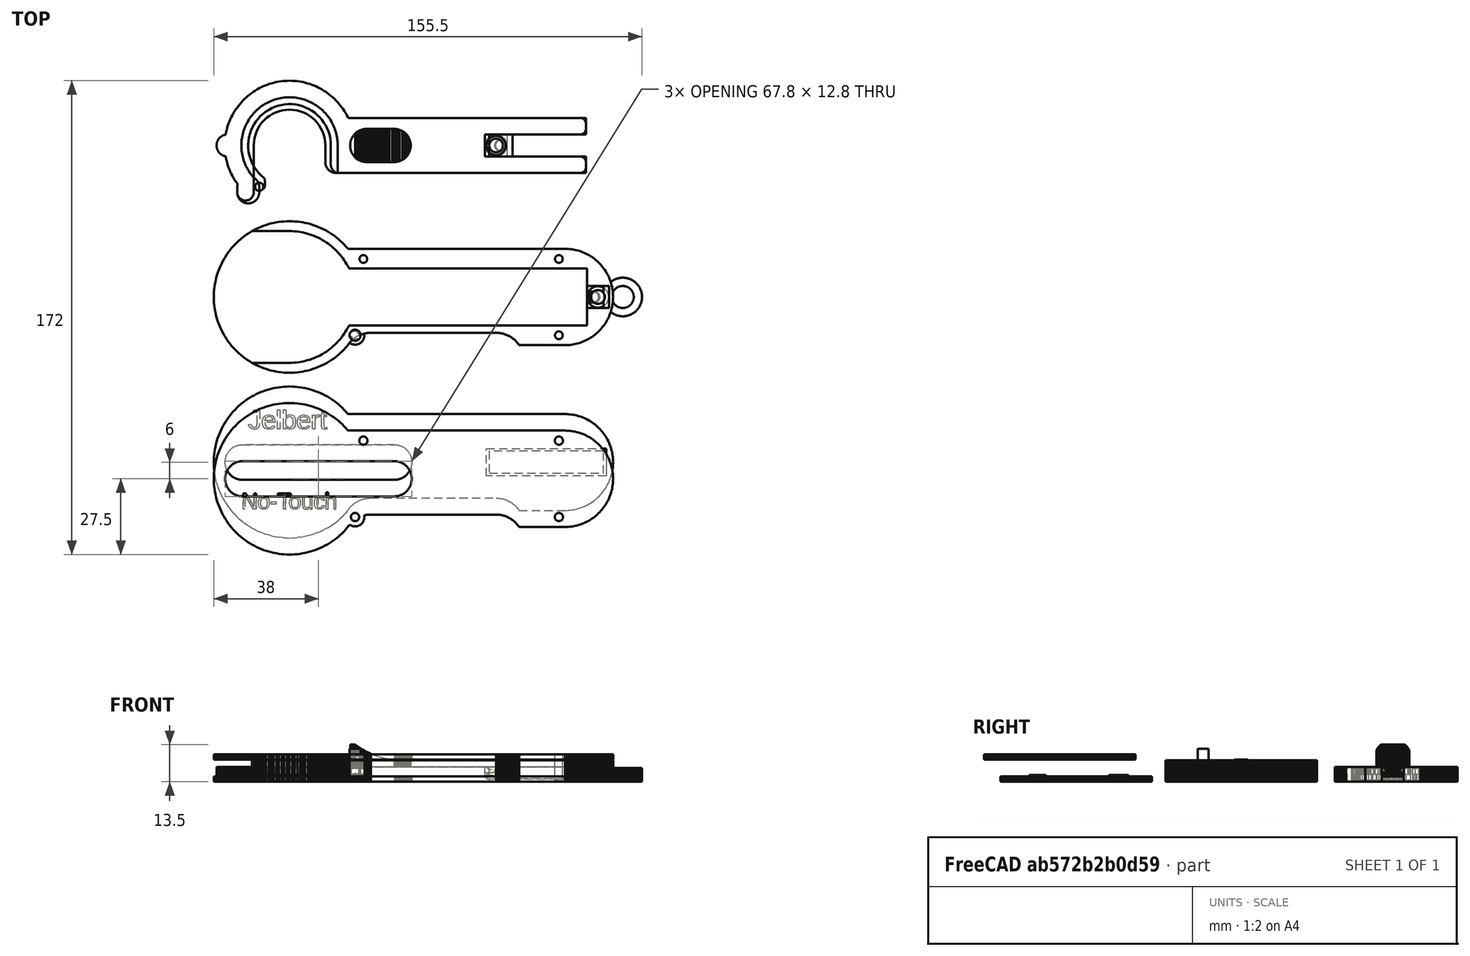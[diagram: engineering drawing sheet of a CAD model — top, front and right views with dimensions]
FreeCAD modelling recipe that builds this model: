
FCSTD DOCUMENT  (FreeCAD 0.18R4 (GitTag))
Label: notouch
License: CreativeCommons Attribution-ShareAlike
LicenseURL: http://creativecommons.org/licenses/by-sa/4.0/
objects: Part::Cylinder×25, Part::Cut×23, Part::Feature×19, Part::MultiFuse×13, Part::Box×13, Part::Fillet×3, Part::Chamfer×3, Part::MultiCommon×2
note: 101 computed .brp shape members not serialized (recipe doc carries the construction recipe); baked Part::Feature solids carry a one-line shape summary decoded from their .brp

FEATURE [Part::Feature] jelbert_no_touch_base_part001_solid001  label="jelbert_no_touch_base_part001 (Solid)001"
  shape: bbox 155.5 x 55 x 7.8 mm, 1307 faces (baked)
FEATURE [Part::Feature] jelbert_no_touch_hook_part001_solid001  label="jelbert_no_touch_hook_part001 (Solid)001"
  shape: bbox 134.1 x 44.5 x 13.5 mm, 1441 faces (baked)
FEATURE [Part::Feature] Cut_solid001  label="jelbert_no_touch_top_part001_01"
  shape: bbox 145 x 55 x 2.5 mm, 996 faces (baked)
FEATURE [Part::Feature] Fusion007002003002  label="soporte_simple014"
  Placement = pos=(91,-56.7,114.8) rot=(0,0,1;0rad)
  shape: bbox 6 x 6 x 6 mm, 8 faces (baked)
FEATURE [Part::Feature] Fusion007002003003  label="soporte_simple015"
  Placement = pos=(20,-56.7,114.8) rot=(0,0,1;0rad)
  shape: bbox 6 x 6 x 6 mm, 8 faces (baked)
FEATURE [Part::Feature] Fusion007002003004  label="soporte_simple016"
  Placement = pos=(91,-84.4,114.8) rot=(0,0,1;0rad)
  shape: bbox 6 x 6 x 6 mm, 8 faces (baked)
FEATURE [Part::Feature] Fusion007002003005  label="soporte_simple017"
  Placement = pos=(17,-84.4,114.8) rot=(0,0,1;0rad)
  shape: bbox 6 x 6 x 6 mm, 8 faces (baked)
FEATURE [Part::Cylinder] Cylinder
  Angle = 360
  AttacherType = Attacher::AttachEngine3D
  Height = 10
  Placement = pos=(26.8,-41.15,2) rot=(0,0,1;0rad)
  Radius = 2
FEATURE [Part::Cylinder] Cylinder001
  Angle = 360
  AttacherType = Attacher::AttachEngine3D
  Height = 10
  Placement = pos=(97.8,-41.15,2) rot=(0,0,1;0rad)
  Radius = 2
FEATURE [Part::Cylinder] Cylinder002
  Angle = 360
  AttacherType = Attacher::AttachEngine3D
  Height = 10
  Placement = pos=(97.8,-68.9,2) rot=(0,0,1;0rad)
  Radius = 2
FEATURE [Part::Cylinder] Cylinder003
  Angle = 360
  AttacherType = Attacher::AttachEngine3D
  Height = 10
  Placement = pos=(23.8,-68.9,2) rot=(0,0,1;0rad)
  Radius = 2
FEATURE [Part::Cylinder] Cylinder004
  Angle = 360
  AttacherType = Attacher::AttachEngine3D
  Height = 7.8
  Placement = pos=(23.8,-68.9,0) rot=(0,0,1;0rad)
  Radius = 3.4
FEATURE [Part::Cylinder] Cylinder005
  Angle = 360
  AttacherType = Attacher::AttachEngine3D
  Height = 10
  Placement = pos=(23.8,-68.9,4) rot=(0,0,1;0rad)
  Radius = 1.5
FEATURE [Part::Feature] jelbert_no_touch_base_part001_solid002  label="jelbert_no_touch_base_part001 (Solid)002"
  shape: bbox 155.5 x 55 x 7.8 mm, 1307 faces (baked)
FEATURE [Part::Cylinder] Cylinder006
  Angle = 360
  AttacherType = Attacher::AttachEngine3D
  Height = 2
  Placement = pos=(23.8,-68.9,8) rot=(0,0,1;0rad)
  Radius = 3.4
FEATURE [Part::MultiFuse] Fusion
  Shapes = -> [jelbert_no_touch_base_part001_solid002,Cylinder004]
FEATURE [Part::Cylinder] Cylinder007
  Angle = 360
  AttacherType = Attacher::AttachEngine3D
  Height = 10
  Placement = pos=(23.8,-68.9,2) rot=(0,0,1;0rad)
  Radius = 2
FEATURE [Part::Cut] Cut
  Base = -> Fusion
  Tool = -> Cylinder003
FEATURE [Part::MultiFuse] Fusion007002003006
  Shapes = -> [Cut,Fusion007002003005]
FEATURE [Part::Cylinder] Cylinder008
  Angle = 360
  AttacherType = Attacher::AttachEngine3D
  Height = 10
  Placement = pos=(26.8,-41.15,2) rot=(0,0,1;0rad)
  Radius = 1.5
FEATURE [Part::Cut] Cut001
  Base = -> Fusion007002003006
  Tool = -> Cylinder
FEATURE [Part::MultiFuse] Fusion007002003007
  Shapes = -> [Cut001,Fusion007002003003]
FEATURE [Part::Cylinder] Cylinder009
  Angle = 360
  AttacherType = Attacher::AttachEngine3D
  Height = 10
  Placement = pos=(97.8,-41.15,3) rot=(0,0,1;0rad)
  Radius = 1.5
FEATURE [Part::Cut] Cut002
  Base = -> Fusion007002003007
  Tool = -> Cylinder001
FEATURE [Part::MultiFuse] Fusion007002003008
  Shapes = -> [Cut002,Fusion007002003002]
FEATURE [Part::Cylinder] Cylinder010
  Angle = 360
  AttacherType = Attacher::AttachEngine3D
  Height = 10
  Placement = pos=(97.8,-68.9,1) rot=(0,0,1;0rad)
  Radius = 1.5
FEATURE [Part::Cut] Cut003
  Base = -> Fusion007002003008
  Tool = -> Cylinder002
FEATURE [Part::MultiFuse] Fusion007002003009  label="base"
  Shapes = -> [Cut003,Fusion007002003004]
FEATURE [Part::Feature] Cut_solid002  label="jelbert_no_touch_top_part001_002"
  shape: bbox 145 x 55 x 2.5 mm, 996 faces (baked)
FEATURE [Part::Box] Box  label="Cube"
  AttacherType = Attacher::AttachEngine3D
  Height = 10
  Length = 175
  Placement = pos=(-39,-152,2) rot=(0,0,1;0rad)
  Width = 67
FEATURE [Part::Cut] Cut004
  Base = -> Cut_solid002
  Tool = -> Box
FEATURE [Part::Box] Box001  label="Cube001"
  AttacherType = Attacher::AttachEngine3D
  Height = 2
  Length = 31
  Placement = pos=(-16,-104,0) rot=(0,0,1;0rad)
  Width = 10
FEATURE [Part::Box] Box002  label="Cube002"
  AttacherType = Attacher::AttachEngine3D
  Height = 2
  Length = 36
  Placement = pos=(-18,-134,0) rot=(0,0,1;0rad)
  Width = 10
FEATURE [Part::Box] Box003  label="Cube003"
  AttacherType = Attacher::AttachEngine3D
  Height = 2
  Length = 45
  Placement = pos=(70,-121,0) rot=(0,0,1;0rad)
  Width = 12
FEATURE [Part::MultiFuse] Fusion007002003010
  Shapes = -> [Cut004,Box001,Box002,Box003]
FEATURE [Part::Feature] Fusion007002003010001  label="tapa_sin_agujeros"
  Placement = pos=(0,60,8) rot=(0,0,1;0rad)
  shape: bbox 145 x 55 x 2 mm, 477 faces (baked)
FEATURE [Part::MultiFuse] Fusion007002003010002  label="tapa_sin_agujeros_1"
  Shapes = -> [Fusion007002003010001,Cylinder006]
FEATURE [Part::Cut] Cut005
  Base = -> Fusion007002003010002
  Tool = -> Cylinder005
FEATURE [Part::Cut] Cut006
  Base = -> Cut005
  Tool = -> Cylinder008
FEATURE [Part::Cut] Cut007
  Base = -> Cut006
  Tool = -> Cylinder009
FEATURE [Part::Cut] Cut008  label="tapa"
  Base = -> Cut007
  Placement = pos=(0,-66,0) rot=(0,0,1;0rad)
  Tool = -> Cylinder010
FEATURE [Part::Feature] jelbert_no_touch_hook_part001_solid002  label="jelbert_no_touch_hook_part001 (Solid)002"
  shape: bbox 134.1 x 44.5 x 13.5 mm, 1441 faces (baked)
FEATURE [Part::Cylinder] Cylinder011
  Angle = 360
  AttacherType = Attacher::AttachEngine3D
  Height = 5.4
  Radius = 18
FEATURE [Part::Cylinder] Cylinder012
  Angle = 360
  AttacherType = Attacher::AttachEngine3D
  Height = 5.4
  Radius = 13
FEATURE [Part::Cut] Cut009
  Base = -> Cylinder011
  Tool = -> Cylinder012
FEATURE [Part::MultiFuse] Fusion007002003010003
  Shapes = -> [jelbert_no_touch_hook_part001_solid002,Cut009]
FEATURE [Part::Box] Box004  label="Cube004"
  AttacherType = Attacher::AttachEngine3D
  Height = 5.4
  Length = 7
  Placement = pos=(15,-10,0) rot=(0,0,1;0rad)
  Width = 7
FEATURE [Part::Cylinder] Cylinder013
  Angle = 360
  AttacherType = Attacher::AttachEngine3D
  Height = 5.4
  Placement = pos=(-11,-15,0) rot=(0,0,1;0rad)
  Radius = 1.5
FEATURE [Part::Feature] Fillet001001  label="medio"
  shape: bbox 134.1 x 44.5 x 13.83 mm, 1304 faces (baked)
FEATURE [Part::Box] Box005  label="Cube005"
  AttacherType = Attacher::AttachEngine3D
  Height = 10
  Length = 24
  Placement = pos=(-9,-21,0) rot=(0,0,1;0rad)
  Width = 21
FEATURE [Part::Cut] Cut010
  Base = -> Fillet001001
  Tool = -> Box005
FEATURE [Part::Fillet] Fillet001002
  Base = -> Cut010
  Edges = 1 edges r=3: [Edge476]
FEATURE [Part::Fillet] Fillet001003
  Base = -> Fillet001002
  Edges = 2 edges r=1: [Edge482,Edge486]
FEATURE [Part::Feature] Fillet001003001  label="medio_final"
  shape: bbox 134.1 x 44.5 x 13.83 mm, 1307 faces (baked)
FEATURE [Part::Cylinder] Cylinder014
  Angle = 360
  AttacherType = Attacher::AttachEngine3D
  Height = 8
  Placement = pos=(112,-55,0) rot=(0,0,1;0rad)
  Radius = 2.5
FEATURE [Part::Box] Box006  label="Cube006"
  AttacherType = Attacher::AttachEngine3D
  Height = 10
  Length = 8
  Placement = pos=(108,-59,4) rot=(0,0,1;0rad)
  Width = 8
FEATURE [Part::Cut] Cut011
  Base = -> Fusion007002003009
  Tool = -> Box006
FEATURE [Part::MultiFuse] Fusion007002003010005
  Shapes = -> [Cut011,Cylinder014]
FEATURE [Part::Feature] Fusion007002003010005001  label="Fusion007002003010006"
  shape: bbox 155.5 x 55 x 8 mm, 665 faces (baked)
FEATURE [Part::Chamfer] Chamfer  label="base_reforzada"
  Base = -> Fusion007002003010005001
  Edges = 1 edges r=1.4: [Edge1928]
FEATURE [Part::Box] Box007  label="Cube007"
  AttacherType = Attacher::AttachEngine3D
  Height = 10
  Length = 8
  Placement = pos=(71,-4,2) rot=(0,0,1;0rad)
  Width = 8
FEATURE [Part::Cylinder] Cylinder015
  Angle = 360
  AttacherType = Attacher::AttachEngine3D
  Height = 5.4
  Placement = pos=(75,0,0) rot=(0,0,1;0rad)
  Radius = 2.5
FEATURE [Part::Cut] Cut012
  Base = -> Fillet001003001
  Tool = -> Box007
FEATURE [Part::Feature] Cut012001  label="Cut013"
  shape: bbox 134.1 x 44.5 x 13.83 mm, 628 faces (baked)
FEATURE [Part::MultiFuse] Fusion007002003010005002
  Shapes = -> [Cut012001,Cylinder015]
FEATURE [Part::Chamfer] Chamfer001  label="Chamfer001_medio_Reforzado"
  Base = -> Fusion007002003010005002
  Edges = 1 edges r=1.4: [Edge2]
FEATURE [Part::Feature] Chamfer001001  label="medio_reforzado"
  shape: bbox 134.1 x 44.5 x 13.83 mm, 631 faces (baked)
FEATURE [Part::Box] Box008  label="Cube008"
  AttacherType = Attacher::AttachEngine3D
  Height = 10
  Length = 26
  Placement = pos=(-13,-21,0) rot=(0,0,1;0rad)
  Width = 21
FEATURE [Part::Cut] Cut012002
  Base = -> Fusion007002003010003
  Tool = -> Box008
FEATURE [Part::MultiFuse] Fusion007002003010005003
  Shapes = -> [Cut012002,Box004]
FEATURE [Part::Cylinder] Cylinder016
  Angle = 360
  AttacherType = Attacher::AttachEngine3D
  Height = 10
  Radius = 8
FEATURE [Part::Cylinder] Cylinder017
  Angle = 360
  AttacherType = Attacher::AttachEngine3D
  Height = 10
  Radius = 4
FEATURE [Part::Cut] Cut012003
  Base = -> Cylinder016
  Tool = -> Cylinder017
FEATURE [Part::Box] Box009  label="Cube009"
  AttacherType = Attacher::AttachEngine3D
  Height = 10
  Length = 10
  Placement = pos=(-10,-10,0) rot=(0,0,1;0rad)
  Width = 10
FEATURE [Part::MultiCommon] Common
  Placement = pos=(17,-6,0) rot=(0,0,1;0rad)
  Shapes = -> [Cut012003,Box009]
FEATURE [Part::Cut] Cut012004
  Base = -> Fusion007002003010005003
  Tool = -> Common
FEATURE [Part::Cylinder] Cylinder018
  Angle = 360
  AttacherType = Attacher::AttachEngine3D
  Height = 10
  Radius = 8
FEATURE [Part::Cylinder] Cylinder019
  Angle = 360
  AttacherType = Attacher::AttachEngine3D
  Height = 10
  Radius = 3
FEATURE [Part::Cut] Cut012005
  Base = -> Cylinder018
  Tool = -> Cylinder019
FEATURE [Part::Box] Box010  label="Cube010"
  AttacherType = Attacher::AttachEngine3D
  Height = 10
  Length = 20
  Placement = pos=(-10,-10,0) rot=(0,0,1;0rad)
  Width = 10
FEATURE [Part::MultiCommon] Common001
  Placement = pos=(-16,-17,0) rot=(0,0,1;0rad)
  Shapes = -> [Cut012005,Box010]
FEATURE [Part::Cut] Cut012006
  Base = -> Cut012004
  Tool = -> Common001
FEATURE [Part::Box] Box011  label="Cube011"
  AttacherType = Attacher::AttachEngine3D
  Height = 10
  Length = 8
  Placement = pos=(71,-4,2) rot=(0,0,1;0rad)
  Width = 8
FEATURE [Part::Cylinder] Cylinder020
  Angle = 360
  AttacherType = Attacher::AttachEngine3D
  Height = 5.4
  Placement = pos=(75,0,0) rot=(0,0,1;0rad)
  Radius = 2.5
FEATURE [Part::Cut] Cut012007
  Base = -> Cut012006
  Tool = -> Box011
FEATURE [Part::MultiFuse] Fusion007002003010005004
  Shapes = -> [Cut012007,Cylinder020]
FEATURE [Part::Feature] Fusion007002003010005004001  label="Fusion007002003010005005"
  shape: bbox 134.1 x 43.5 x 13.5 mm, 536 faces (baked)
FEATURE [Part::Chamfer] Chamfer001002
  Base = -> Fusion007002003010005004001
  Edges = 1 edges r=1.4: [Edge772]
FEATURE [Part::Fillet] Fillet  label="medio_reforzado_v2"
  Base = -> Chamfer001002
  Edges = 4 edges r=2: [Edge21,Edge25,Edge599,Edge600]
FEATURE [Part::Cylinder] Cylinder021
  Angle = 360
  AttacherType = Attacher::AttachEngine3D
  Height = 10
  Placement = pos=(97.8,-41.2,0.4) rot=(0,0,1;0rad)
  Radius = 1.4
FEATURE [Part::Cylinder] Cylinder022
  Angle = 360
  AttacherType = Attacher::AttachEngine3D
  Height = 10
  Placement = pos=(26.8,-41.2,0.4) rot=(0,0,1;0rad)
  Radius = 1.4
FEATURE [Part::Cylinder] Cylinder023
  Angle = 360
  AttacherType = Attacher::AttachEngine3D
  Height = 10
  Placement = pos=(23.8,-68.9,0.4) rot=(0,0,1;0rad)
  Radius = 1.4
FEATURE [Part::Cylinder] Cylinder024
  Angle = 360
  AttacherType = Attacher::AttachEngine3D
  Height = 10
  Placement = pos=(97.8,-68.9,0.4) rot=(0,0,1;0rad)
  Radius = 1.4
FEATURE [Part::Cut] Cut012008
  Base = -> Chamfer
  Tool = -> Cylinder024
FEATURE [Part::Cut] Cut012009
  Base = -> Cut012008
  Tool = -> Cylinder021
FEATURE [Part::Cut] Cut012010
  Base = -> Cut012009
  Tool = -> Cylinder022
FEATURE [Part::Cut] Cut012011
  Base = -> Cut012010
  Tool = -> Cylinder023
FEATURE [Part::Feature] Cut012011001  label="base_reforzado_v2"
  shape: bbox 155.5 x 55 x 8 mm, 669 faces (baked)
FEATURE [Part::Box] Box012  label="Cube012"
  AttacherType = Attacher::AttachEngine3D
  Height = 1
  Length = 10
  Placement = pos=(71,-4,2.4) rot=(0,0,1;0rad)
  Width = 8
FEATURE [Part::Feature] Common002001  label="Common003"
  Placement = pos=(150,0,7.8) rot=(0,1,0;3.14159rad)
  shape: bbox 7 x 7 x 1 mm, 6 faces (baked)
FEATURE [Part::MultiFuse] Fusion007002003010005004002  label="medio_reforzado_v2.1"
  Shapes = -> [Fillet,Common002001]
